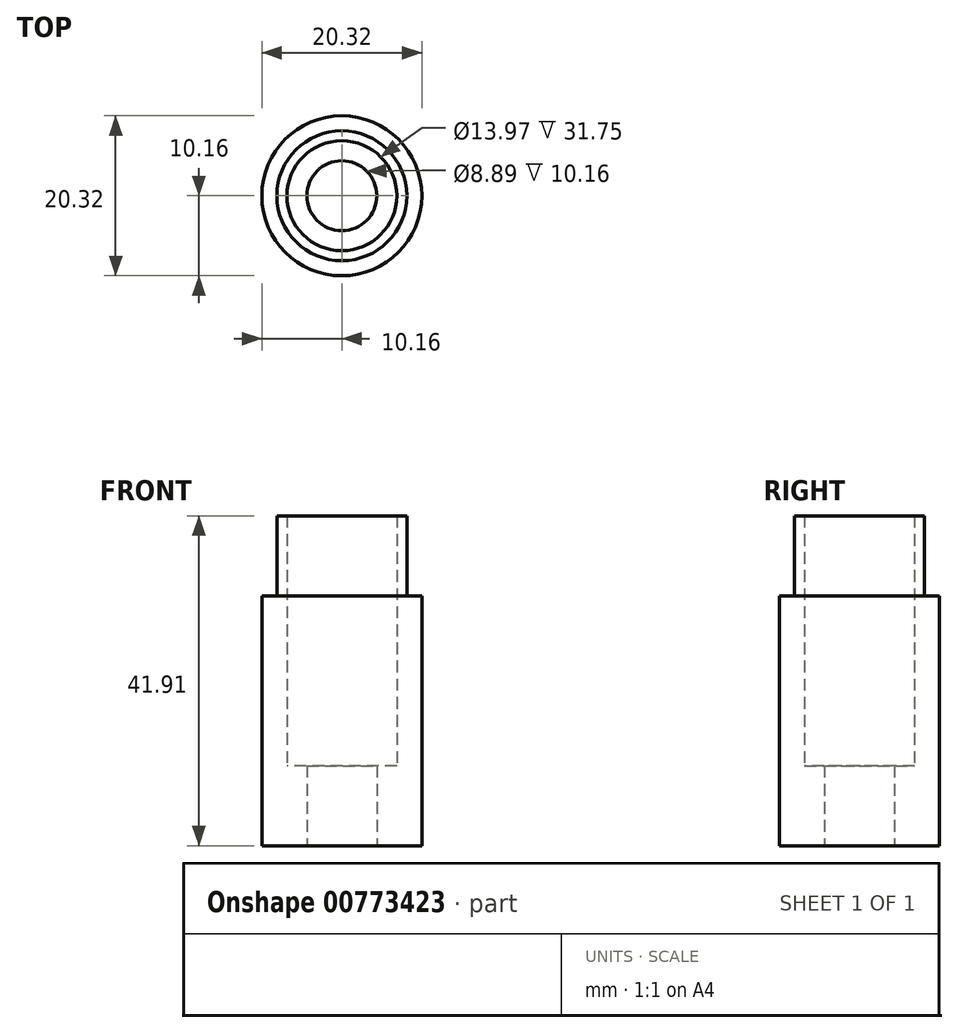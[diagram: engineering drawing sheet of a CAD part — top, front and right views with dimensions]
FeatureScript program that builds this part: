
annotation { "Feature Type Name" : "Feature", "Feature Type Description" : "" }
export const myFeature = defineFeature(function(context is Context, id is Id, definition is map)
    precondition{}
    {
        {
            var Q0;
            Q0=qCreatedBy(makeId("Top.planeOp"),FACE);
            var sketch = newSketch(context, id + "F0", { "sketchPlane" : qUnion([Q0])});
            skCircle(sketch, "E0", {"center": v(0, 0) * mm, "radius": 10.16 * mm});
            skCircle(sketch, "E1", {"center": v(0, 0) * mm, "radius": 6.99 * mm});
            skSolve(sketch);
        }
        {
            var Q0;
            Q0=makeQuery(id+"F0.imprint","IMPRINT",FACE,{"disambiguationData":[TD([[makeQuery(id+"F0.imprint","IMPRINT",EDGE,{"derivedFrom":sQuery(id+"F0.wireOp",EDGE,"E0")}),1.0]])]});
            extrude(context, id + "F1", {"entities" : qUnion([Q0]), "depth" : 31.75 * mm});
        }
        {
            var Q0;
            Q0=makeQuery(id+"F1.opExtrude","CAP_FACE",FACE,{"disambiguationData":[OSD([sQuery(id+"F0.wireOp",EDGE,"E0"),sQuery(id+"F0.wireOp",EDGE,"E1")])],"isStart":false});
            var sketch = newSketch(context, id + "F2", { "sketchPlane" : qUnion([Q0])});
            skCircle(sketch, "E2", {"center": v(0, 0) * mm, "radius": 8.26 * mm});
            skSolve(sketch);
        }
        {
            var Q0;
            Q0=makeQuery(id+"F2.imprint","IMPRINT",FACE,{"disambiguationData":[TD([[makeQuery(id+"F2.imprint","IMPRINT",EDGE,{"derivedFrom":sQuery(id+"F2.wireOp",EDGE,"E2")}),1.0]])]});
            extrude(context, id + "F3", {"entities" : qUnion([Q0]), "operationType" : NewBodyOperationType.ADD, "depth" : 10.16 * mm});
        }
        {
            var Q0;
            Q0=makeQuery(id+"F1.opExtrude","CAP_FACE",FACE,{"disambiguationData":[OSD([sQuery(id+"F0.wireOp",EDGE,"E0"),sQuery(id+"F0.wireOp",EDGE,"E1")])],"isStart":true});
            var sketch = newSketch(context, id + "F4", { "sketchPlane" : qUnion([Q0])});
            skCircle(sketch, "E3", {"center": v(0, 0) * mm, "radius": 4.45 * mm});
            skSolve(sketch);
        }
        {
            var Q0;
            Q0=makeQuery(id+"F4.imprint","IMPRINT",FACE,{"disambiguationData":[TD([[makeQuery(id+"F4.imprint","IMPRINT",EDGE,{"derivedFrom":sQuery(id+"F4.wireOp",EDGE,"E3")}),-1.0]])]});
            extrude(context, id + "F5", {"entities" : qUnion([Q0]), "operationType" : NewBodyOperationType.ADD, "oppositeDirection" : true, "depth" : 10.16 * mm});
        }
    });
